# Revit family: Erdungs-Systeme_Verbindungs_und_Anschlussmaterial_Erdungs-Anschlussblock
name_source: partatom
category: Generic Models
revit_build: Autodesk Revit 2015 (Build: 20140606_1530(x64)
units: mm (PartAtom-declared; Revit-internal decimal feet)

## types (6) — shared parameters
B = 51 mm  [stored 0.167323 ft]
Diameter dimesion = 11 mm  [stored 0.0360892 ft]
Height = 50 mm  [stored 0.164042 ft]
Manufacturer = OBO Bettermann
Size "a" = 50 mm  [stored 0.164042 ft]
Size "b" = 22 mm  [stored 0.0721785 ft]
URL = http://www.obo-bettermann.com
Width = 50 mm  [stored 0.164042 ft]

## per-type parameters (varying)
| type | "A" Dimension | GTIN | Manufacturer Art. No. | Material | Outer width |
| 1805 2 FT | 110 mm  [stored 0.360892 ft] | 4012195379096 | 5016029 | Steel, Galvanized | 155 mm  [stored 0.50853 ft] |
| 1805 4 FT | 212 mm  [stored 0.695538 ft] | 4012195379157 | 5016037 | Steel, Galvanized | 257 mm  [stored 0.843176 ft] |
| 1805 4 VA | 212 mm  [stored 0.695538 ft] | 4012195800354 | 5016118 | Stainless Steel AISI 304 | 257 mm  [stored 0.843176 ft] |
| 1805 2 VA | 110 mm  [stored 0.360892 ft] | 4012195922216 | 5016096 | Stainless Steel AISI 304 | 155 mm  [stored 0.50853 ft] |
| 1805 6 VA | 314 mm  [stored 1.03018 ft] | 4012195922278 | 5016126 | Stainless Steel AISI 304 | 359 mm  [stored 1.17782 ft] |
| 1805 6 FT | 314 mm  [stored 1.03018 ft] | 4012195379218 | 5016045 | Steel, Galvanized | 359 mm  [stored 1.17782 ft] |

note: column(s) folded — value = type name in every type: Article Type

note: [stored X ft] marks values corroborated as IEEE doubles in the binary element streams (Revit-internal decimal feet)

## geometry (parser evidence)
native form markers: Sweep x1
no freeform markers — native parametric forms only
